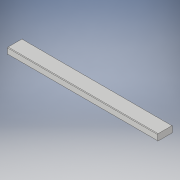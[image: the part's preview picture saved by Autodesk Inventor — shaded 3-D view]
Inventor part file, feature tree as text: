
AUTODESK INVENTOR PART (.ipt)
format: ipt  version: 2019 (Build 230136000, 136)  size: 101,376 bytes
history: native  units: in
note: dims shown in document units (in); Inventor stores cm internally (conversion verified against a paired STEP export)
features: extrude x1, fillet x1, sketch x1
ambient origin geometry x8: Origin, YZ Plane, XZ Plane, XY Plane, X Axis, Y Axis, Z Axis, Center Point
bodies: Solid1 (feature_tree)
feature tree (3):
  extrude  "Extrusion1"  Depth=3.5in
  fillet  "Fillet1"  Radius=35.4331in
  sketch  "Sketch1"  dims[d0=1.5in d1=3.5in d2=35.4331in d3=0.0in d4=0.125in]
